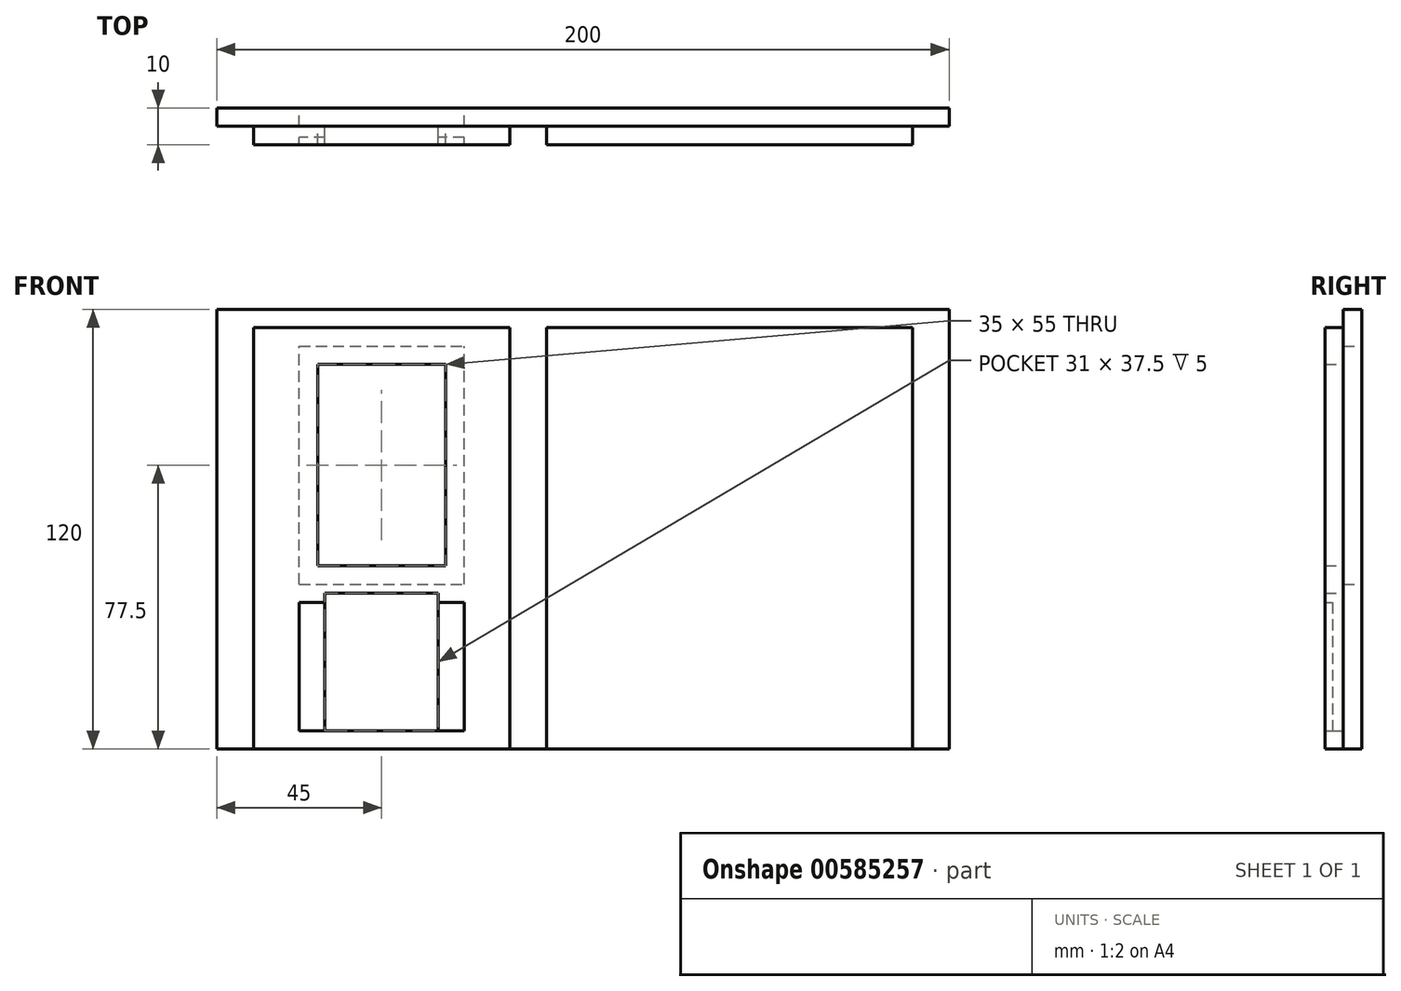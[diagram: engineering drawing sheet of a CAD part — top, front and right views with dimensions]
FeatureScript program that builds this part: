
annotation { "Feature Type Name" : "Feature", "Feature Type Description" : "" }
export const myFeature = defineFeature(function(context is Context, id is Id, definition is map)
    precondition{}
    {
        {
            var Q0;
            Q0=qCreatedBy(makeId("Front.planeOp"),FACE);
            var sketch = newSketch(context, id + "F0", { "sketchPlane" : qUnion([Q0])});
            skLineSegment(sketch, "E0.top", {"start": v(-100, 60) * mm, "end": v(100, 60) * mm});
            skLineSegment(sketch, "E0.left", {"start": v(-100, -60) * mm, "end": v(-100, 60) * mm});
            skLineSegment(sketch, "E0.right", {"start": v(100, -60) * mm, "end": v(100, 60) * mm});
            skPoint(sketch, "E0.middle", {"position": v(0, 0) * mm});
            skLineSegment(sketch, "E1", {"start": v(-100, -60) * mm, "end": v(-90, -60) * mm});
            skLineSegment(sketch, "E2", {"start": v(-90, -60) * mm, "end": v(-20, -60) * mm});
            skLineSegment(sketch, "E3", {"start": v(-20, -60) * mm, "end": v(-10, -60) * mm});
            skLineSegment(sketch, "E4", {"start": v(-10, -60) * mm, "end": v(90, -60) * mm});
            skLineSegment(sketch, "E5", {"start": v(90, -60) * mm, "end": v(100, -60) * mm});
            skLineSegment(sketch, "E6", {"start": v(-90, -60) * mm, "end": v(-90, 55) * mm});
            skLineSegment(sketch, "E7", {"start": v(-90, 55) * mm, "end": v(-20, 55) * mm});
            skLineSegment(sketch, "E8", {"start": v(-20, 55) * mm, "end": v(-20, -60) * mm});
            skLineSegment(sketch, "E9", {"start": v(-10, -60) * mm, "end": v(-10, 55) * mm});
            skLineSegment(sketch, "E10", {"start": v(-10, 55) * mm, "end": v(90, 55) * mm});
            skLineSegment(sketch, "E11", {"start": v(90, 55) * mm, "end": v(90, -60) * mm});
            skLineSegment(sketch, "E12.left", {"start": v(-77.5, -55) * mm, "end": v(-77.5, -20) * mm});
            skLineSegment(sketch, "E12.right", {"start": v(-32.5, -55) * mm, "end": v(-32.5, -20) * mm});
            skPoint(sketch, "E12.middle", {"position": v(-55, -37.5) * mm});
            skLineSegment(sketch, "E13", {"start": v(-77.5, -20) * mm, "end": v(-70.5, -20) * mm});
            skLineSegment(sketch, "E14", {"start": v(-39.5, -20) * mm, "end": v(-32.5, -20) * mm});
            skLineSegment(sketch, "E15", {"start": v(-32.5, -55) * mm, "end": v(-39.5, -55) * mm});
            skLineSegment(sketch, "E16", {"start": v(-39.5, -55) * mm, "end": v(-70.5, -55) * mm});
            skLineSegment(sketch, "E17", {"start": v(-70.5, -55) * mm, "end": v(-77.5, -55) * mm});
            skLineSegment(sketch, "E18", {"start": v(-70.5, -20) * mm, "end": v(-70.5, -55) * mm});
            skLineSegment(sketch, "E19", {"start": v(-39.5, -20) * mm, "end": v(-39.5, -55) * mm});
            skPoint(sketch, "E20.middle", {"position": v(-55, 17.5) * mm});
            skLineSegment(sketch, "E21.bottom", {"start": v(-77.5, -15) * mm, "end": v(-32.5, -15) * mm});
            skLineSegment(sketch, "E21.top", {"start": v(-77.5, 50) * mm, "end": v(-32.5, 50) * mm});
            skLineSegment(sketch, "E21.left", {"start": v(-77.5, -15) * mm, "end": v(-77.5, 50) * mm});
            skLineSegment(sketch, "E21.right", {"start": v(-32.5, -15) * mm, "end": v(-32.5, 50) * mm});
            skLineSegment(sketch, "E22.bottom", {"start": v(-72.5, -10) * mm, "end": v(-37.5, -10) * mm});
            skLineSegment(sketch, "E22.top", {"start": v(-72.5, 45) * mm, "end": v(-37.5, 45) * mm});
            skLineSegment(sketch, "E22.left", {"start": v(-72.5, -10) * mm, "end": v(-72.5, 45) * mm});
            skLineSegment(sketch, "E22.right", {"start": v(-37.5, -10) * mm, "end": v(-37.5, 45) * mm});
            skLineSegment(sketch, "E23.bottom", {"start": v(-70.5, -20) * mm, "end": v(-39.5, -20) * mm});
            skLineSegment(sketch, "E23.right", {"start": v(-39.5, -20) * mm, "end": v(-39.5, -20) * mm});
            skLineSegment(sketch, "E24.top", {"start": v(-70.5, -17.5) * mm, "end": v(-39.5, -17.5) * mm});
            skLineSegment(sketch, "E24.left", {"start": v(-70.5, -20) * mm, "end": v(-70.5, -17.5) * mm});
            skLineSegment(sketch, "E24.right", {"start": v(-39.5, -20) * mm, "end": v(-39.5, -17.5) * mm});
            skSolve(sketch);
        }
        {
            var Q0;
            Q0=makeQuery(id+"F0.imprint","IMPRINT",FACE,{"disambiguationData":[TD([[makeQuery(id+"F0.imprint","IMPRINT",EDGE,{"derivedFrom":sQuery(id+"F0.wireOp",EDGE,"E0.top")}),-1.0]])]});
            extrude(context, id + "F1", {"entities" : qUnion([Q0]), "depth" : 5 * mm, "offsetDistance" : 25 * mm});
        }
        {
            var Q0;
            Q0=makeQuery(id+"F0.imprint","IMPRINT",FACE,{"disambiguationData":[TD([[makeQuery(id+"F0.imprint","IMPRINT",EDGE,{"derivedFrom":sQuery(id+"F0.wireOp",EDGE,"E2")}),1.0]])]});
            var Q1;
            Q1=makeQuery(id+"F0.imprint","IMPRINT",FACE,{"disambiguationData":[TD([[makeQuery(id+"F0.imprint","IMPRINT",EDGE,{"derivedFrom":sQuery(id+"F0.wireOp",EDGE,"E4")}),1.0]])]});
            extrude(context, id + "F2", {"entities" : qUnion([Q0, Q1]), "operationType" : NewBodyOperationType.ADD, "depth" : 10 * mm, "offsetDistance" : 25 * mm});
        }
        {
            var Q0;
            Q0=makeQuery(id+"F0.imprint","IMPRINT",FACE,{"disambiguationData":[TD([[makeQuery(id+"F0.imprint","IMPRINT",EDGE,{"derivedFrom":sQuery(id+"F0.wireOp",EDGE,"E21.bottom")}),1.0]])]});
            extrude(context, id + "F3", {"entities" : qUnion([Q0]), "operationType" : NewBodyOperationType.ADD, "depth" : 10 * mm, "offsetDistance" : 25 * mm});
        }
        {
            var Q0;
            Q0=makeQuery(id+"F0.imprint","IMPRINT",FACE,{"disambiguationData":[TD([[makeQuery(id+"F0.imprint","IMPRINT",EDGE,{"derivedFrom":sQuery(id+"F0.wireOp",EDGE,"E21.bottom")}),1.0]])]});
            extrude(context, id + "F4", {"entities" : qUnion([Q0]), "operationType" : NewBodyOperationType.REMOVE, "oppositeDirection" : true, "depth" : -5 * mm, "offsetDistance" : 25 * mm});
        }
        {
            var Q0;
            Q0=makeQuery(id+"F0.imprint","IMPRINT",FACE,{"disambiguationData":[TD([[makeQuery(id+"F0.imprint","IMPRINT",EDGE,{"derivedFrom":sQuery(id+"F0.wireOp",EDGE,"E12.left")}),-1.0]])]});
            var Q1;
            Q1=makeQuery(id+"F0.imprint","IMPRINT",FACE,{"disambiguationData":[TD([[makeQuery(id+"F0.imprint","IMPRINT",EDGE,{"derivedFrom":sQuery(id+"F0.wireOp",EDGE,"E12.right")}),1.0]])]});
            extrude(context, id + "F5", {"entities" : qUnion([Q0, Q1]), "operationType" : NewBodyOperationType.ADD, "depth" : 8 * mm, "offsetDistance" : 25 * mm});
        }
        {
            var Q0;
            Q0=makeQuery(id+"F0.imprint","IMPRINT",FACE,{"disambiguationData":[TD([[makeQuery(id+"F0.imprint","IMPRINT",EDGE,{"derivedFrom":sQuery(id+"F0.wireOp",EDGE,"E16")}),-1.0]])]});
            extrude(context, id + "F6", {"entities" : qUnion([Q0]), "operationType" : NewBodyOperationType.ADD, "depth" : 5 * mm, "offsetDistance" : 25 * mm});
        }
        {
            var Q0;
            Q0=makeQuery(id+"F0.imprint","IMPRINT",FACE,{"disambiguationData":[TD([[makeQuery(id+"F0.imprint","IMPRINT",EDGE,{"derivedFrom":sQuery(id+"F0.wireOp",EDGE,"E23.bottom")}),1.0]])]});
            extrude(context, id + "F7", {"entities" : qUnion([Q0]), "operationType" : NewBodyOperationType.ADD, "depth" : 5 * mm, "offsetDistance" : 25 * mm});
        }
    });
